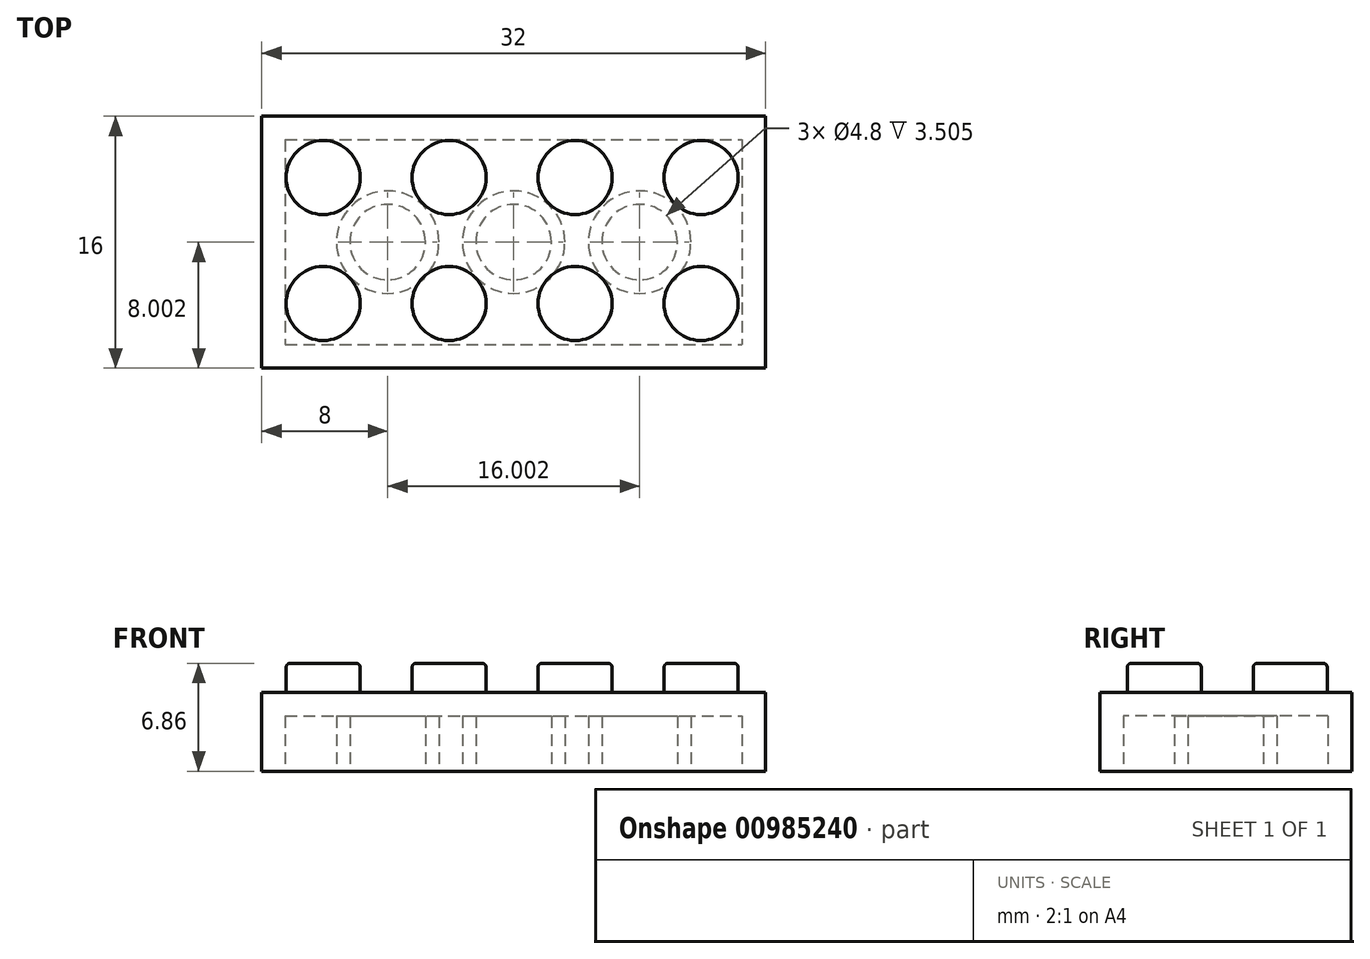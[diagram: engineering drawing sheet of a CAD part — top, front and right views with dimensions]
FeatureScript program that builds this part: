
annotation { "Feature Type Name" : "Feature", "Feature Type Description" : "" }
export const myFeature = defineFeature(function(context is Context, id is Id, definition is map)
    precondition{}
    {
        {
            var Q0;
            Q0=qCreatedBy(makeId("Top.planeOp"),FACE);
            var sketch = newSketch(context, id + "F0", { "sketchPlane" : qUnion([Q0])});
            skLineSegment(sketch, "E0.bottom", {"start": v(-55.01, 16.96) * mm, "end": v(-23, 16.96) * mm});
            skLineSegment(sketch, "E0.top", {"start": v(-55.01, 0.96) * mm, "end": v(-23, 0.96) * mm});
            skLineSegment(sketch, "E0.left", {"start": v(-55.01, 16.96) * mm, "end": v(-55.01, 0.96) * mm});
            skLineSegment(sketch, "E0.right", {"start": v(-23, 16.96) * mm, "end": v(-23, 0.96) * mm});
            skSolve(sketch);
        }
        {
            var Q0;
            Q0=makeQuery(id+"F0.imprint","IMPRINT",FACE,{"disambiguationData":[TD([[makeQuery(id+"F0.imprint","IMPRINT",EDGE,{"derivedFrom":sQuery(id+"F0.wireOp",EDGE,"E0.bottom")}),-1.0]])]});
            extrude(context, id + "F1", {"entities" : qUnion([Q0]), "depth" : 5 * mm, "offsetDistance" : 25.4 * mm});
        }
        {
            var Q0;
            Q0=makeQuery(id+"F1.opExtrude","CAP_FACE",FACE,{"disambiguationData":[OSD([sQuery(id+"F0.wireOp",EDGE,"E0.bottom"),sQuery(id+"F0.wireOp",EDGE,"E0.top"),sQuery(id+"F0.wireOp",EDGE,"E0.left"),sQuery(id+"F0.wireOp",EDGE,"E0.right")])],"isStart":false});
            var sketch = newSketch(context, id + "F2", { "sketchPlane" : qUnion([Q0])});
            skCircle(sketch, "E1", {"center": v(-51.11, 13.06) * mm, "radius": 2.35 * mm});
            skCircle(sketch, "E2.0.1.0", {"center": v(-51.11, 5.06) * mm, "radius": 2.35 * mm});
            skCircle(sketch, "E2.1.0.0", {"center": v(-43.11, 13.06) * mm, "radius": 2.35 * mm});
            skCircle(sketch, "E2.1.1.0", {"center": v(-43.11, 5.06) * mm, "radius": 2.35 * mm});
            skCircle(sketch, "E2.2.0.0", {"center": v(-35.11, 13.06) * mm, "radius": 2.35 * mm});
            skCircle(sketch, "E2.2.1.0", {"center": v(-35.11, 5.06) * mm, "radius": 2.35 * mm});
            skCircle(sketch, "E2.3.0.0", {"center": v(-27.1, 13.06) * mm, "radius": 2.35 * mm});
            skCircle(sketch, "E2.3.1.0", {"center": v(-27.1, 5.06) * mm, "radius": 2.35 * mm});
            skLineSegment(sketch, "E2.direction1", {"start": v(-51.11, 13.06) * mm, "end": v(-43.11, 13.06) * mm, "construction": true});
            skLineSegment(sketch, "E2.direction2", {"start": v(-51.11, 13.06) * mm, "end": v(-51.11, 5.06) * mm, "construction": true});
            skSolve(sketch);
        }
        {
            var Q0;
            Q0=makeQuery(id+"F2.imprint","IMPRINT",FACE,{"disambiguationData":[TD([[makeQuery(id+"F2.imprint","IMPRINT",EDGE,{"derivedFrom":sQuery(id+"F2.wireOp",EDGE,"E1")}),1.0]])]});
            var Q1;
            Q1=makeQuery(id+"F2.imprint","IMPRINT",FACE,{"disambiguationData":[TD([[makeQuery(id+"F2.imprint","IMPRINT",EDGE,{"derivedFrom":sQuery(id+"F2.wireOp",EDGE,"E2.1.0.0")}),1.0]])]});
            var Q2;
            Q2=makeQuery(id+"F2.imprint","IMPRINT",FACE,{"disambiguationData":[TD([[makeQuery(id+"F2.imprint","IMPRINT",EDGE,{"derivedFrom":sQuery(id+"F2.wireOp",EDGE,"E2.2.0.0")}),1.0]])]});
            var Q3;
            Q3=makeQuery(id+"F2.imprint","IMPRINT",FACE,{"disambiguationData":[TD([[makeQuery(id+"F2.imprint","IMPRINT",EDGE,{"derivedFrom":sQuery(id+"F2.wireOp",EDGE,"E2.3.0.0")}),1.0]])]});
            var Q4;
            Q4=makeQuery(id+"F2.imprint","IMPRINT",FACE,{"disambiguationData":[TD([[makeQuery(id+"F2.imprint","IMPRINT",EDGE,{"derivedFrom":sQuery(id+"F2.wireOp",EDGE,"E2.3.1.0")}),1.0]])]});
            var Q5;
            Q5=makeQuery(id+"F2.imprint","IMPRINT",FACE,{"disambiguationData":[TD([[makeQuery(id+"F2.imprint","IMPRINT",EDGE,{"derivedFrom":sQuery(id+"F2.wireOp",EDGE,"E2.2.1.0")}),1.0]])]});
            var Q6;
            Q6=makeQuery(id+"F2.imprint","IMPRINT",FACE,{"disambiguationData":[TD([[makeQuery(id+"F2.imprint","IMPRINT",EDGE,{"derivedFrom":sQuery(id+"F2.wireOp",EDGE,"E2.1.1.0")}),1.0]])]});
            var Q7;
            Q7=makeQuery(id+"F2.imprint","IMPRINT",FACE,{"disambiguationData":[TD([[makeQuery(id+"F2.imprint","IMPRINT",EDGE,{"derivedFrom":sQuery(id+"F2.wireOp",EDGE,"E2.0.1.0")}),1.0]])]});
            extrude(context, id + "F3", {"entities" : qUnion([Q0, Q1, Q2, Q3, Q4, Q5, Q6, Q7]), "operationType" : NewBodyOperationType.ADD, "depth" : 1.85 * mm, "offsetDistance" : 25.4 * mm});
        }
        {
            var Q0;
            Q0=makeQuery(id+"F3.opExtrude","CAP_EDGE",EDGE,{"disambiguationData":[OSD([sQuery(id+"F2.wireOp",EDGE,"E2.0.1.0")])],"isStart":false});
            var Q1;
            Q1=makeQuery(id+"F3.opExtrude","CAP_EDGE",EDGE,{"disambiguationData":[OSD([sQuery(id+"F2.wireOp",EDGE,"E1")])],"isStart":false});
            var Q2;
            Q2=makeQuery(id+"F3.opExtrude","CAP_EDGE",EDGE,{"disambiguationData":[OSD([sQuery(id+"F2.wireOp",EDGE,"E2.1.0.0")])],"isStart":false});
            var Q3;
            Q3=makeQuery(id+"F3.opExtrude","CAP_EDGE",EDGE,{"disambiguationData":[OSD([sQuery(id+"F2.wireOp",EDGE,"E2.1.1.0")])],"isStart":false});
            var Q4;
            Q4=makeQuery(id+"F3.opExtrude","CAP_EDGE",EDGE,{"disambiguationData":[OSD([sQuery(id+"F2.wireOp",EDGE,"E2.2.1.0")])],"isStart":false});
            var Q5;
            Q5=makeQuery(id+"F3.opExtrude","CAP_EDGE",EDGE,{"disambiguationData":[OSD([sQuery(id+"F2.wireOp",EDGE,"E2.2.0.0")])],"isStart":false});
            var Q6;
            Q6=makeQuery(id+"F3.opExtrude","CAP_EDGE",EDGE,{"disambiguationData":[OSD([sQuery(id+"F2.wireOp",EDGE,"E2.3.0.0")])],"isStart":false});
            var Q7;
            Q7=makeQuery(id+"F3.opExtrude","CAP_EDGE",EDGE,{"disambiguationData":[OSD([sQuery(id+"F2.wireOp",EDGE,"E2.3.1.0")])],"isStart":false});
            fillet(context, id + "F4", {"entities" : qUnion([Q0, Q1, Q2, Q3, Q4, Q5, Q6, Q7]), "radius" : 0.25 * mm, "tangentPropagation" : true, "allowEdgeOverflow" : false});
        }
        {
            var Q0;
            Q0=makeQuery(id+"F1.opExtrude","CAP_FACE",FACE,{"disambiguationData":[OSD([sQuery(id+"F0.wireOp",EDGE,"E0.bottom"),sQuery(id+"F0.wireOp",EDGE,"E0.top"),sQuery(id+"F0.wireOp",EDGE,"E0.left"),sQuery(id+"F0.wireOp",EDGE,"E0.right")])],"isStart":true});
            var sketch = newSketch(context, id + "F5", { "sketchPlane" : qUnion([Q0])});
            skLineSegment(sketch, "E3.0", {"start": v(-53.51, -2.46) * mm, "end": v(-24.5, -2.46) * mm});
            skLineSegment(sketch, "E3.1", {"start": v(-53.51, -15.46) * mm, "end": v(-53.51, -2.46) * mm});
            skLineSegment(sketch, "E3.2", {"start": v(-53.51, -15.46) * mm, "end": v(-24.5, -15.46) * mm});
            skLineSegment(sketch, "E3.3", {"start": v(-24.5, -15.46) * mm, "end": v(-24.5, -2.46) * mm});
            skLineSegment(sketch, "E4", {"start": v(-55.01, -0.96) * mm, "end": v(-23, -16.96) * mm, "construction": true});
            skLineSegment(sketch, "E5", {"start": v(-23, -16.96) * mm, "end": v(-23, -0.96) * mm});
            skLineSegment(sketch, "E6", {"start": v(-23, -0.96) * mm, "end": v(-55.01, -16.96) * mm, "construction": true});
            skCircle(sketch, "E7", {"center": v(-39, -8.96) * mm, "radius": 3.25 * mm});
            skCircle(sketch, "E8", {"center": v(-39, -8.96) * mm, "radius": 2.4 * mm});
            skCircle(sketch, "E9", {"center": v(-47.01, -8.96) * mm, "radius": 3.25 * mm});
            skCircle(sketch, "E10", {"center": v(-47.01, -8.96) * mm, "radius": 2.4 * mm});
            skCircle(sketch, "E11", {"center": v(-31, -8.96) * mm, "radius": 3.25 * mm});
            skCircle(sketch, "E12", {"center": v(-31, -8.96) * mm, "radius": 2.4 * mm});
            skSolve(sketch);
        }
        {
            var Q0;
            Q0=makeQuery(id+"F5.imprint","IMPRINT",FACE,{"disambiguationData":[TD([[makeQuery(id+"F5.imprint","IMPRINT",EDGE,{"derivedFrom":sQuery(id+"F5.wireOp",EDGE,"E3.0")}),-1.0]])]});
            var Q1;
            Q1=makeQuery(id+"F5.imprint","IMPRINT",FACE,{"disambiguationData":[TD([[makeQuery(id+"F5.imprint","IMPRINT",EDGE,{"derivedFrom":sQuery(id+"F5.wireOp",EDGE,"E10")}),1.0]])]});
            var Q2;
            Q2=makeQuery(id+"F5.imprint","IMPRINT",FACE,{"disambiguationData":[TD([[makeQuery(id+"F5.imprint","IMPRINT",EDGE,{"derivedFrom":sQuery(id+"F5.wireOp",EDGE,"E8")}),1.0]])]});
            var Q3;
            Q3=makeQuery(id+"F5.imprint","IMPRINT",FACE,{"disambiguationData":[TD([[makeQuery(id+"F5.imprint","IMPRINT",EDGE,{"derivedFrom":sQuery(id+"F5.wireOp",EDGE,"E12")}),1.0]])]});
            extrude(context, id + "F6", {"entities" : qUnion([Q0, Q1, Q2, Q3]), "operationType" : NewBodyOperationType.REMOVE, "oppositeDirection" : true, "depth" : 3.5 * mm, "offsetDistance" : 25.4 * mm});
        }
    });
